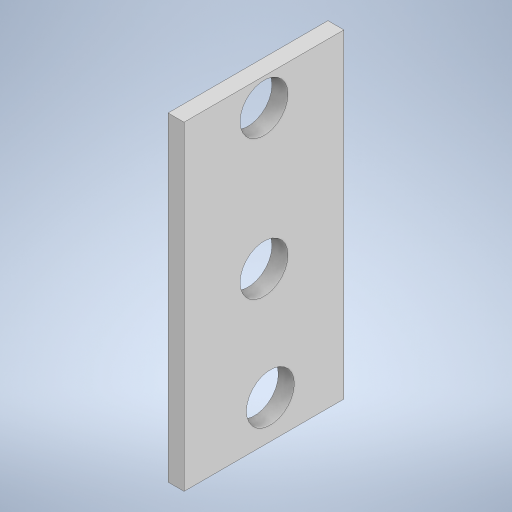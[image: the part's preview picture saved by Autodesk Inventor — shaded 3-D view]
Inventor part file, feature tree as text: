
AUTODESK INVENTOR PART (.ipt)
format: ipt  version: 2023 (Build 270158000, 158)  size: 231,424 bytes
history: native  units: in
note: dims shown in document units (in); Inventor stores cm internally (conversion verified against a paired STEP export)
features: sketch x2, extrude x1, hole x1
ambient origin geometry x8: Origin, YZ Plane, XZ Plane, XY Plane, X Axis, Y Axis, Z Axis, Center Point
bodies: Solid1 (feature_tree)
feature tree (4):
  extrude  "Extrusion1"  Depth=0.3937in
  hole  "Hole1"  [1 undecoded]
  sketch  "Sketch1"  dims[d0=0.7874in d1=0.3937in]
  sketch  "Sketch2"  dims[d2=0.0394in d3=0.0in d4=0.1181in d5=0.1181in d6=0.1181in d7=0.1181in d8=0.2953in d9=0.1476in d10=0.0984in d11=90.0deg d12=0.3937in d13=0.8108in d14=0.2953in d15=0.8108in d16=0.0246in d17=0.2953in d18=0.1476in]
note: 1 required parameter value undecoded (feature->parameter linkage not recoverable at this tier; creation-order binding heuristic only, values carry confidence <= 0.55)
